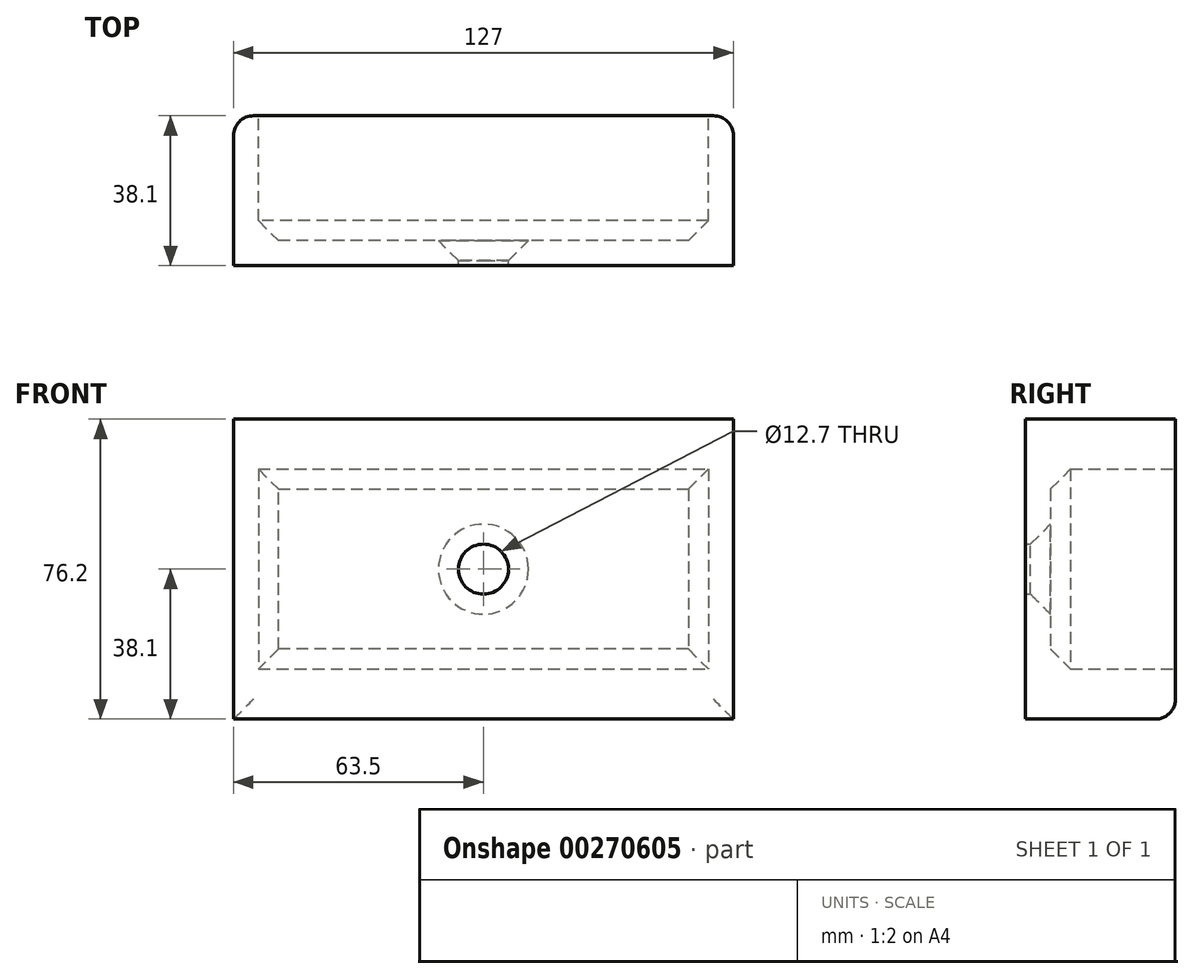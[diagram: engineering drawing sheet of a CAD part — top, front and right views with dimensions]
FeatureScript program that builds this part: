
annotation { "Feature Type Name" : "Feature", "Feature Type Description" : "" }
export const myFeature = defineFeature(function(context is Context, id is Id, definition is map)
    precondition{}
    {
        {
            var Q0;
            Q0=qCreatedBy(makeId("Front.planeOp"),FACE);
            var sketch = newSketch(context, id + "F0", { "sketchPlane" : qUnion([Q0])});
            skLineSegment(sketch, "E0.bottom", {"start": v(63.5, 38.1) * mm, "end": v(-63.5, 38.1) * mm});
            skLineSegment(sketch, "E0.top", {"start": v(63.5, -38.1) * mm, "end": v(-63.5, -38.1) * mm});
            skLineSegment(sketch, "E0.left", {"start": v(63.5, 38.1) * mm, "end": v(63.5, -38.1) * mm});
            skLineSegment(sketch, "E0.right", {"start": v(-63.5, 38.1) * mm, "end": v(-63.5, -38.1) * mm});
            skPoint(sketch, "E0.middle", {"position": v(0, 0) * mm});
            skSolve(sketch);
        }
        {
            var Q0;
            Q0=makeQuery(id+"F0.imprint","IMPRINT",FACE,{"disambiguationData":[TD([[makeQuery(id+"F0.imprint","IMPRINT",EDGE,{"derivedFrom":sQuery(id+"F0.wireOp",EDGE,"E0.bottom")}),1.0]])]});
            extrude(context, id + "F1", {"entities" : qUnion([Q0]), "depth" : 38.1 * mm});
        }
        {
            var Q0;
            Q0=qCreatedBy(makeId("Front.planeOp"),FACE);
            var sketch = newSketch(context, id + "F2", { "sketchPlane" : qUnion([Q0])});
            skCircle(sketch, "E1", {"center": v(0, 0) * mm, "radius": 6.35 * mm});
            skSolve(sketch);
        }
        {
            var Q0;
            Q0=makeQuery(id+"F2.imprint","IMPRINT",FACE,{"disambiguationData":[TD([[makeQuery(id+"F2.imprint","IMPRINT",EDGE,{"derivedFrom":sQuery(id+"F2.wireOp",EDGE,"E1")}),1.0]])]});
            extrude(context, id + "F3", {"entities" : qUnion([Q0]), "operationType" : NewBodyOperationType.REMOVE, "depth" : 50.8 * mm});
        }
        {
            var Q0;
            Q0=makeQuery(id+"F1.opExtrude","CAP_EDGE",EDGE,{"disambiguationData":[OSD([sQuery(id+"F0.wireOp",EDGE,"E0.left")])],"isStart":true});
            var Q1;
            Q1=makeQuery(id+"F1.opExtrude","CAP_EDGE",EDGE,{"disambiguationData":[OSD([sQuery(id+"F0.wireOp",EDGE,"E0.top")])],"isStart":true});
            var Q2;
            Q2=makeQuery(id+"F1.opExtrude","CAP_EDGE",EDGE,{"disambiguationData":[OSD([sQuery(id+"F0.wireOp",EDGE,"E0.right")])],"isStart":true});
            fillet(context, id + "F4", {"entities" : qUnion([Q0, Q1, Q2]), "radius" : 5.08 * mm, "tangentPropagation" : true, "allowEdgeOverflow" : false});
        }
        {
            var Q0;
            Q0=qCreatedBy(makeId("Front.planeOp"),FACE);
            var sketch = newSketch(context, id + "F5", { "sketchPlane" : qUnion([Q0])});
            skLineSegment(sketch, "E2.bottom", {"start": v(-57.15, 25.4) * mm, "end": v(57.15, 25.4) * mm});
            skLineSegment(sketch, "E2.top", {"start": v(-57.15, -25.4) * mm, "end": v(57.15, -25.4) * mm});
            skLineSegment(sketch, "E2.left", {"start": v(-57.15, 25.4) * mm, "end": v(-57.15, -25.4) * mm});
            skLineSegment(sketch, "E2.right", {"start": v(57.15, 25.4) * mm, "end": v(57.15, -25.4) * mm});
            skPoint(sketch, "E2.middle", {"position": v(0, 0) * mm});
            skSolve(sketch);
        }
        {
            var Q0;
            Q0=makeQuery(id+"F5.imprint","IMPRINT",FACE,{"disambiguationData":[TD([[makeQuery(id+"F5.imprint","IMPRINT",EDGE,{"derivedFrom":sQuery(id+"F5.wireOp",EDGE,"E2.bottom")}),-1.0]])]});
            extrude(context, id + "F6", {"entities" : qUnion([Q0]), "operationType" : NewBodyOperationType.REMOVE, "depth" : 31.75 * mm});
        }
        {
            var Q0;
            Q0=makeQuery(id+"F6.boolean.opBoolean","INTERSECT",EDGE,{"derivedFrom":[makeQuery(id+"F3.boolean.opBoolean","COPY",FACE,{"derivedFrom":makeQuery(id+"F3.opExtrude","SWEPT_FACE",FACE,{"disambiguationData":[OSD([sQuery(id+"F2.wireOp",EDGE,"E1")])]})}),makeQuery(id+"F6.opExtrude","CAP_FACE",FACE,{"disambiguationData":[OSD([sQuery(id+"F5.wireOp",EDGE,"E2.bottom"),sQuery(id+"F5.wireOp",EDGE,"E2.top"),sQuery(id+"F5.wireOp",EDGE,"E2.left"),sQuery(id+"F5.wireOp",EDGE,"E2.right")])],"isStart":false})]});
            var Q1;
            Q1=makeQuery(id+"F6.boolean.opBoolean","COPY",FACE,{"derivedFrom":makeQuery(id+"F6.opExtrude","CAP_FACE",FACE,{"disambiguationData":[OSD([sQuery(id+"F5.wireOp",EDGE,"E2.bottom"),sQuery(id+"F5.wireOp",EDGE,"E2.top"),sQuery(id+"F5.wireOp",EDGE,"E2.left"),sQuery(id+"F5.wireOp",EDGE,"E2.right")])],"isStart":false})});
            chamfer(context, id + "F7", {"entities" : qUnion([Q0, Q1]), "width" : 5.08 * mm, "tangentPropagation" : true});
        }
    });
